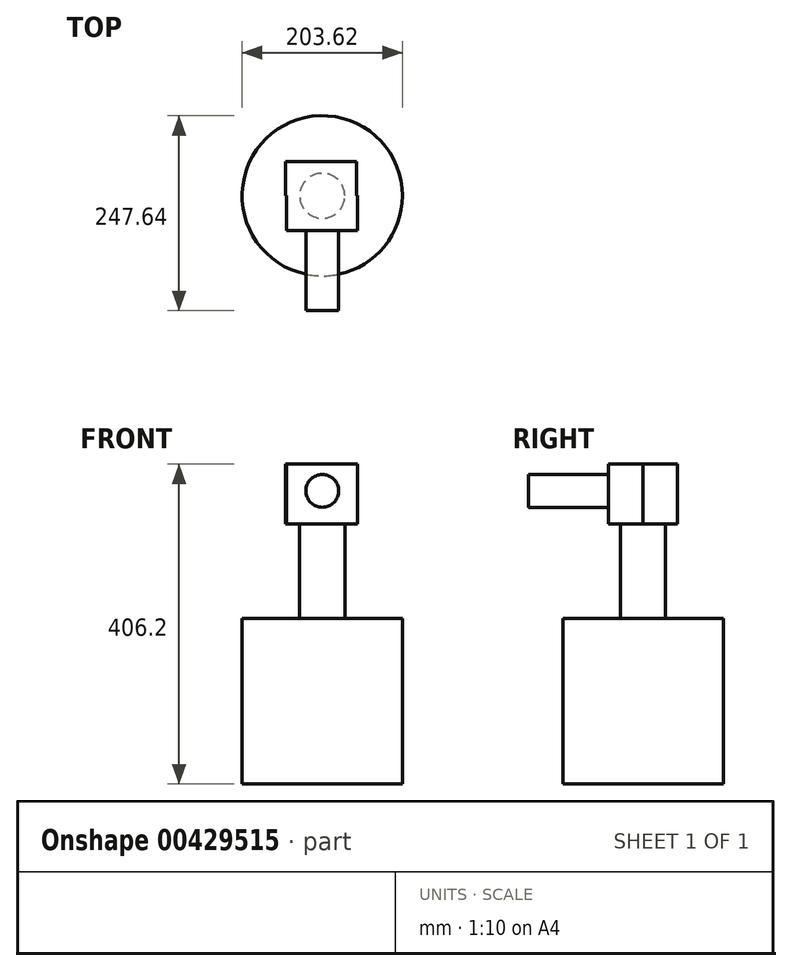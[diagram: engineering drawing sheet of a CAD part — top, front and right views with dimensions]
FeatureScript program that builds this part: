
annotation { "Feature Type Name" : "Feature", "Feature Type Description" : "" }
export const myFeature = defineFeature(function(context is Context, id is Id, definition is map)
    precondition{}
    {
        {
            var Q0;
            Q0=qCreatedBy(makeId("Top.planeOp"),FACE);
            var sketch = newSketch(context, id + "F0", { "sketchPlane" : qUnion([Q0])});
            skCircle(sketch, "E0", {"center": v(0, 0) * mm, "radius": 101.8 * mm});
            skSolve(sketch);
        }
        {
            var Q0;
            Q0=makeQuery(id+"F0.imprint","IMPRINT",FACE,{"disambiguationData":[TD([[makeQuery(id+"F0.imprint","IMPRINT",EDGE,{"derivedFrom":sQuery(id+"F0.wireOp",EDGE,"E0")}),1.0]])]});
            extrude(context, id + "F1", {"entities" : qUnion([Q0]), "depth" : 160 * mm});
        }
        {
            var Q0;
            Q0=makeQuery(id+"F1.opExtrude","CAP_FACE",FACE,{"disambiguationData":[OSD([sQuery(id+"F0.wireOp",EDGE,"E0")])],"isStart":false});
            var sketch = newSketch(context, id + "F2", { "sketchPlane" : qUnion([Q0])});
            skCircle(sketch, "E1", {"center": v(0, 0) * mm, "radius": 28.58 * mm});
            skSolve(sketch);
        }
        {
            var Q0;
            Q0=makeQuery(id+"F2.imprint","IMPRINT",FACE,{"disambiguationData":[TD([[makeQuery(id+"F2.imprint","IMPRINT",EDGE,{"derivedFrom":sQuery(id+"F2.wireOp",EDGE,"E1")}),1.0]])]});
            var Q1;
            Q1=qSketchRegion(id+"F2",true);
            extrude(context, id + "F3", {"entities" : qUnion([Q0, Q1]), "operationType" : NewBodyOperationType.ADD, "depth" : 120 * mm});
        }
        {
            var Q0;
            Q0=makeQuery(id+"F1.opExtrude","CAP_FACE",FACE,{"disambiguationData":[OSD([sQuery(id+"F0.wireOp",EDGE,"E0")])],"isStart":true});
            extrude(context, id + "F4", {"entities" : qUnion([Q0]), "operationType" : NewBodyOperationType.ADD, "depth" : 50 * mm});
        }
        {
            var Q0;
            Q0=makeQuery(id+"F3.opExtrude","CAP_FACE",FACE,{"disambiguationData":[OSD([sQuery(id+"F2.wireOp",EDGE,"E1")])],"isStart":false});
            var sketch = newSketch(context, id + "F5", { "sketchPlane" : qUnion([Q0])});
            skCircle(sketch, "E2", {"center": v(0, 0) * mm, "radius": 36.86 * mm});
            skLineSegment(sketch, "E3", {"start": v(5.83, -36.4) * mm, "end": v(0, 36.86) * mm});
            skSolve(sketch);
        }
        {
            var Q0;
            Q0=qSketchRegion(id+"F5",true);
            var sketch = newSketch(context, id + "F6", { "sketchPlane" : qUnion([Q0])});
            skLineSegment(sketch, "E4.bottom", {"start": v(44.7, 0) * mm, "end": v(-45.43, 0) * mm});
            skLineSegment(sketch, "E4.top", {"start": v(44.7, -44.23) * mm, "end": v(-45.43, -44.23) * mm});
            skLineSegment(sketch, "E4.left", {"start": v(44.7, 0) * mm, "end": v(44.7, -44.23) * mm});
            skLineSegment(sketch, "E4.right", {"start": v(-45.43, 0) * mm, "end": v(-45.43, -44.23) * mm});
            skSolve(sketch);
        }
        {
            var Q0;
            Q0=qSketchRegion(id+"F5",true);
            var sketch = newSketch(context, id + "F7", { "sketchPlane" : qUnion([Q0])});
            skLineSegment(sketch, "E5.bottom", {"start": v(43.64, 0) * mm, "end": v(-46.8, 0) * mm});
            skLineSegment(sketch, "E5.top", {"start": v(43.64, 43.64) * mm, "end": v(-46.8, 43.64) * mm});
            skLineSegment(sketch, "E5.left", {"start": v(43.64, 0) * mm, "end": v(43.64, 43.64) * mm});
            skLineSegment(sketch, "E5.right", {"start": v(-46.8, 0) * mm, "end": v(-46.8, 43.64) * mm});
            skSolve(sketch);
        }
        {
            var Q0;
            Q0=qSketchRegion(id+"F6",true);
            var Q1;
            Q1=qSketchRegion(id+"F7",true);
            extrude(context, id + "F8", {"entities" : qUnion([Q0, Q1]), "operationType" : NewBodyOperationType.ADD, "depth" : 76.2 * mm});
        }
        {
            var Q0;
            Q0=makeQuery(id+"F8.opExtrude","SWEPT_FACE",FACE,{"disambiguationData":[OSD([sQuery(id+"F6.wireOp",EDGE,"E4.top")])]});
            var sketch = newSketch(context, id + "F9", { "sketchPlane" : qUnion([Q0])});
            skCircle(sketch, "E6", {"center": v(0, 322.2) * mm, "radius": 20.79 * mm});
            skSolve(sketch);
        }
        {
            var Q0;
            Q0=makeQuery(id+"F9.imprint","IMPRINT",FACE,{"disambiguationData":[TD([[makeQuery(id+"F9.imprint","IMPRINT",EDGE,{"derivedFrom":sQuery(id+"F9.wireOp",EDGE,"E6")}),1.0]])]});
            extrude(context, id + "F10", {"entities" : qUnion([Q0]), "operationType" : NewBodyOperationType.ADD, "depth" : 101.6 * mm});
        }
    });
